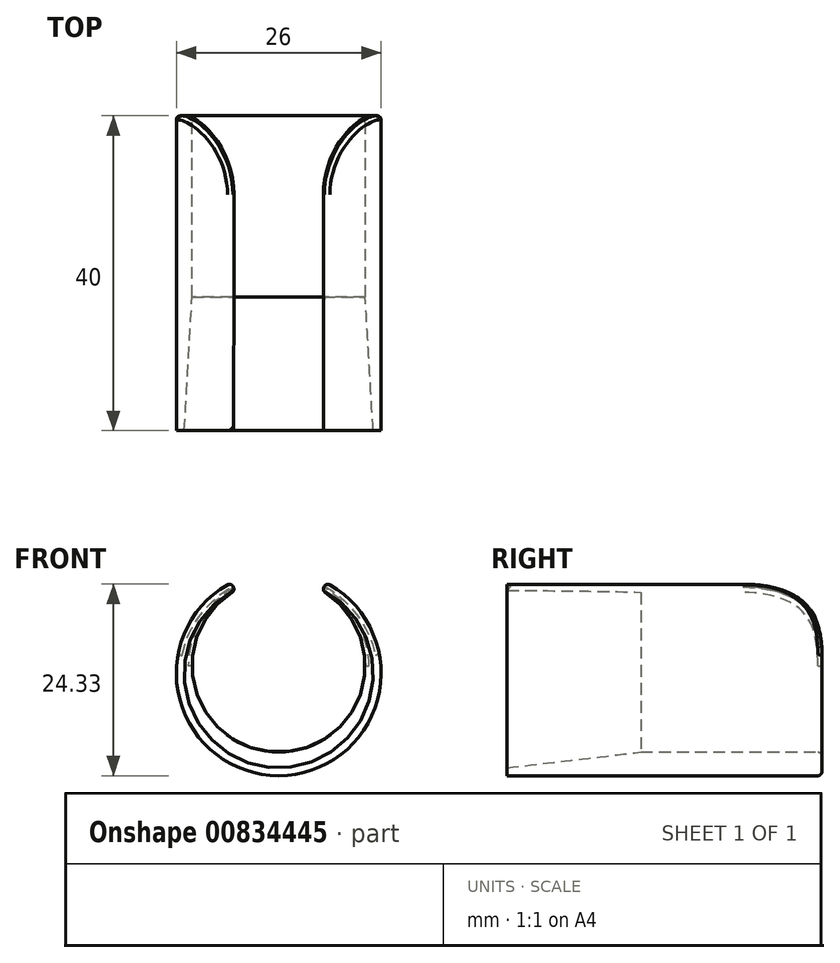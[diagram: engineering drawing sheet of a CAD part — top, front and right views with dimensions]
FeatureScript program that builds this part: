
annotation { "Feature Type Name" : "Feature", "Feature Type Description" : "" }
export const myFeature = defineFeature(function(context is Context, id is Id, definition is map)
    precondition{}
    {
        {
            var Q0;
            Q0=qCreatedBy(makeId("Front.planeOp"),FACE);
            var sketch = newSketch(context, id + "F0", { "sketchPlane" : qUnion([Q0])});
            skPoint(sketch, "E0", {"position": v(0, -1) * mm});
            skLineSegment(sketch, "E1", {"start": v(0, 0) * mm, "end": v(-5.5, 9.53) * mm, "construction": true});
            skLineSegment(sketch, "E2", {"start": v(0, 0) * mm, "end": v(11.48, 19.88) * mm, "construction": true});
            skArc(sketch, "E3", {"start": v(-5.5, 9.53) * mm, "mid": v(0, -11) * mm, "end": v(5.5, 9.53) * mm});
            skArc(sketch, "E4", {"start": v(-5.56, 9.63) * mm, "mid": v(0, -13) * mm, "end": v(5.56, 9.63) * mm});
            skArc(sketch, "E5", {"start": v(-6.06, 10.5) * mm, "mid": v(0, -14) * mm, "end": v(6.06, 10.5) * mm});
            skLineSegment(sketch, "E6", {"start": v(5.5, 9.53) * mm, "end": v(6.06, 10.5) * mm});
            skLineSegment(sketch, "E7.trimOffspring", {"start": v(-6.06, 10.5) * mm, "end": v(-11.9, 20.6) * mm, "construction": true});
            skLineSegment(sketch, "E8", {"start": v(-6.06, 10.5) * mm, "end": v(-5.5, 9.53) * mm});
            skSolve(sketch);
        }
        {
            var Q0;
            {var subQ0=sQuery(id+"F0.wireOp",EDGE,"E4");Q0=makeQuery(id+"F0.imprint","IMPRINT",FACE,{"disambiguationData":[TD([[makeQuery(id+"F0.imprint","IMPRINT",EDGE,{"derivedFrom":subQ0}),-1.0]])]});}
            var Q1;
            {var subQ0=sQuery(id+"F0.wireOp",EDGE,"E3");Q1=makeQuery(id+"F0.imprint","IMPRINT",FACE,{"disambiguationData":[TD([[makeQuery(id+"F0.imprint","IMPRINT",EDGE,{"derivedFrom":subQ0}),-1.0]])]});}
            extrude(context, id + "F1", {"entities" : qUnion([Q0, Q1]), "depth" : 23 * mm, "offsetDistance" : 25 * mm});
        }
        {
            var Q0;
            {var subQ0=sQuery(id+"F0.wireOp",EDGE,"E4");Q0=makeQuery(id+"F0.imprint","IMPRINT",FACE,{"disambiguationData":[TD([[makeQuery(id+"F0.imprint","IMPRINT",EDGE,{"derivedFrom":subQ0}),-1.0]])]});}
            extrude(context, id + "F2", {"entities" : qUnion([Q0]), "depth" : 40 * mm, "offsetDistance" : 25 * mm, "hasSecondDirection" : true, "secondDirectionOppositeDirection" : false, "secondDirectionDepth" : 40 * mm});
        }
        {
            var Q1;
            Q1=makeQuery(id+"F1.opExtrude","CAP_FACE",FACE,{"disambiguationData":[OSD([sQuery(id+"F0.wireOp",EDGE,"E3"),sQuery(id+"F0.wireOp",EDGE,"E5"),sQuery(id+"F0.wireOp",EDGE,"E6"),sQuery(id+"F0.wireOp",EDGE,"E8")])],"isStart":false});
            var Q2;
            Q2=makeQuery(id+"F2.opExtrude","CAP_FACE",FACE,{"disambiguationData":[OSD([sQuery(id+"F0.wireOp",EDGE,"E4"),sQuery(id+"F0.wireOp",EDGE,"E5"),sQuery(id+"F0.wireOp",EDGE,"E6"),sQuery(id+"F0.wireOp",EDGE,"E8")])],"isStart":true});
            loft(context, id + "F3", {"operationType" : NewBodyOperationType.ADD, "sheetProfilesArray" : [{ "sheetProfileEntities" : qUnion([Q1]) }, { "sheetProfileEntities" : qUnion([Q2]) }]});
        }
        {
            var Q0;
            Q0=makeQuery(id+"F3.opLoft","MID_CAP_EDGE",EDGE,{"disambiguationData":[OSD([sQuery(id+"F0.wireOp",EDGE,"E4"),sQuery(id+"F0.wireOp",EDGE,"E5"),sQuery(id+"F0.wireOp",EDGE,"E8")])],"capPos":1.0});
            var Q1;
            Q1=makeQuery(id+"F3.opLoft","MID_CAP_EDGE",EDGE,{"disambiguationData":[OSD([sQuery(id+"F0.wireOp",EDGE,"E4"),sQuery(id+"F0.wireOp",EDGE,"E5"),sQuery(id+"F0.wireOp",EDGE,"E6")])],"capPos":1.0});
            var Q2;
            Q2=makeQuery(id+"F1.opExtrude","CAP_EDGE",EDGE,{"disambiguationData":[OSD([sQuery(id+"F0.wireOp",EDGE,"E6")])],"isStart":true});
            var Q3;
            Q3=makeQuery(id+"F1.opExtrude","CAP_EDGE",EDGE,{"disambiguationData":[OSD([sQuery(id+"F0.wireOp",EDGE,"E8")])],"isStart":true});
            fillet(context, id + "F4", {"entities" : qUnion([Q0, Q1, Q2, Q3]), "radius" : 10 * mm, "tangentPropagation" : true, "allowEdgeOverflow" : false});
        }
        {
            var Q0;
            {var subQ0=sQuery(id+"F0.wireOp",EDGE,"E8");Q0=makeQuery(id+"F3.boolean.opBoolean","MERGE",FACE,{"derivedFrom":[makeQuery(id+"F1.opExtrude","SWEPT_FACE",FACE,{"disambiguationData":[OSD([subQ0])]}),makeQuery(id+"F3.opLoft","SWEPT_FACE",FACE,{"disambiguationData":[OSD([sQuery(id+"F0.wireOp",EDGE,"E3"),sQuery(id+"F0.wireOp",EDGE,"E4"),sQuery(id+"F0.wireOp",EDGE,"E5"),subQ0])]})]});}
            fillet(context, id + "F5", {"entities" : qUnion([Q0]), "radius" : 0.5 * mm, "tangentPropagation" : true, "allowEdgeOverflow" : false});
        }
    });
